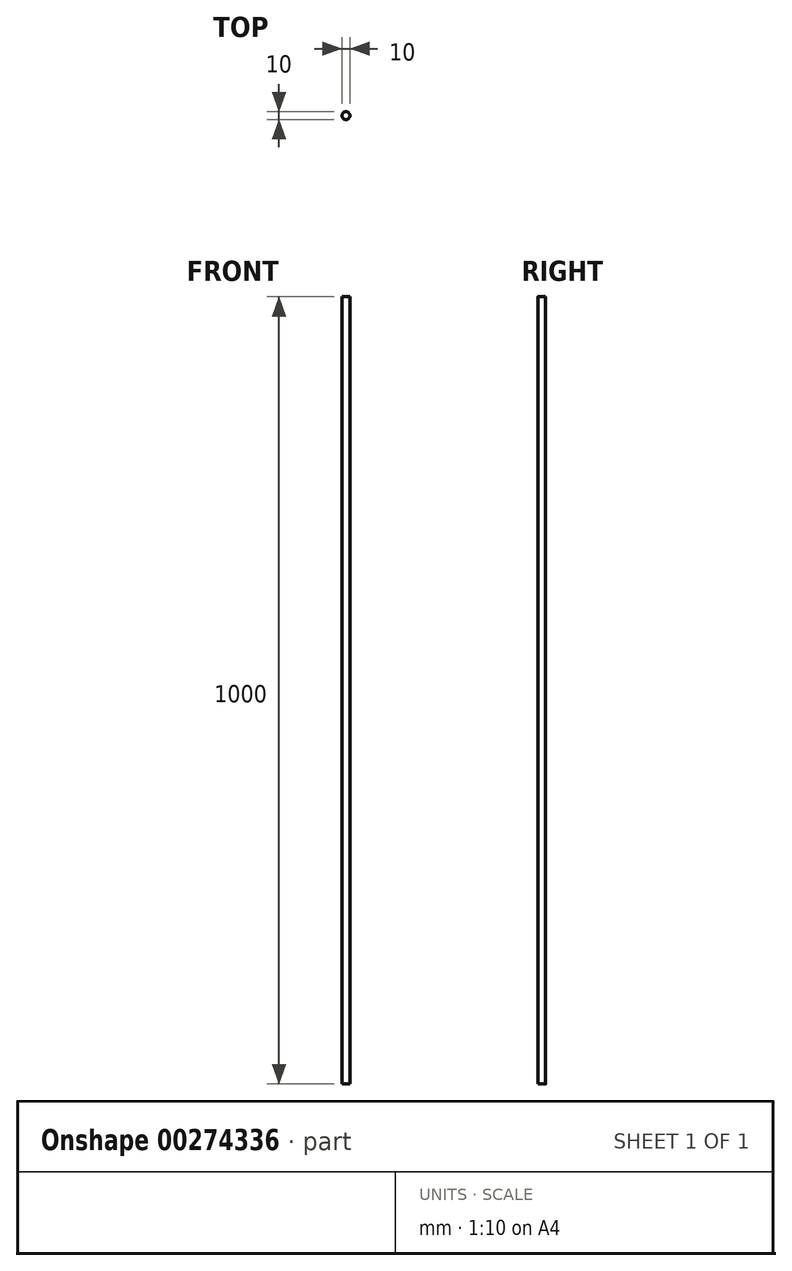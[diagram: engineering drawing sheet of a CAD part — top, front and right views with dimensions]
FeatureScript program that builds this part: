
annotation { "Feature Type Name" : "Feature", "Feature Type Description" : "" }
export const myFeature = defineFeature(function(context is Context, id is Id, definition is map)
    precondition{}
    {
        {
            var Q0;
            Q0=qCreatedBy(makeId("Top.planeOp"),FACE);
            var sketch = newSketch(context, id + "F0", { "sketchPlane" : qUnion([Q0])});
            skCircle(sketch, "E0", {"center": v(0, 0) * mm, "radius": 5 * mm});
            skSolve(sketch);
        }
        {
            var Q0;
            Q0=makeQuery(id+"F0.imprint","IMPRINT",FACE,{"disambiguationData":[TD([[makeQuery(id+"F0.imprint","IMPRINT",EDGE,{"derivedFrom":sQuery(id+"F0.wireOp",EDGE,"E0")}),1.0]])]});
            extrude(context, id + "F1", {"entities" : qUnion([Q0]), "depth" : 1000 * mm});
        }
    });
